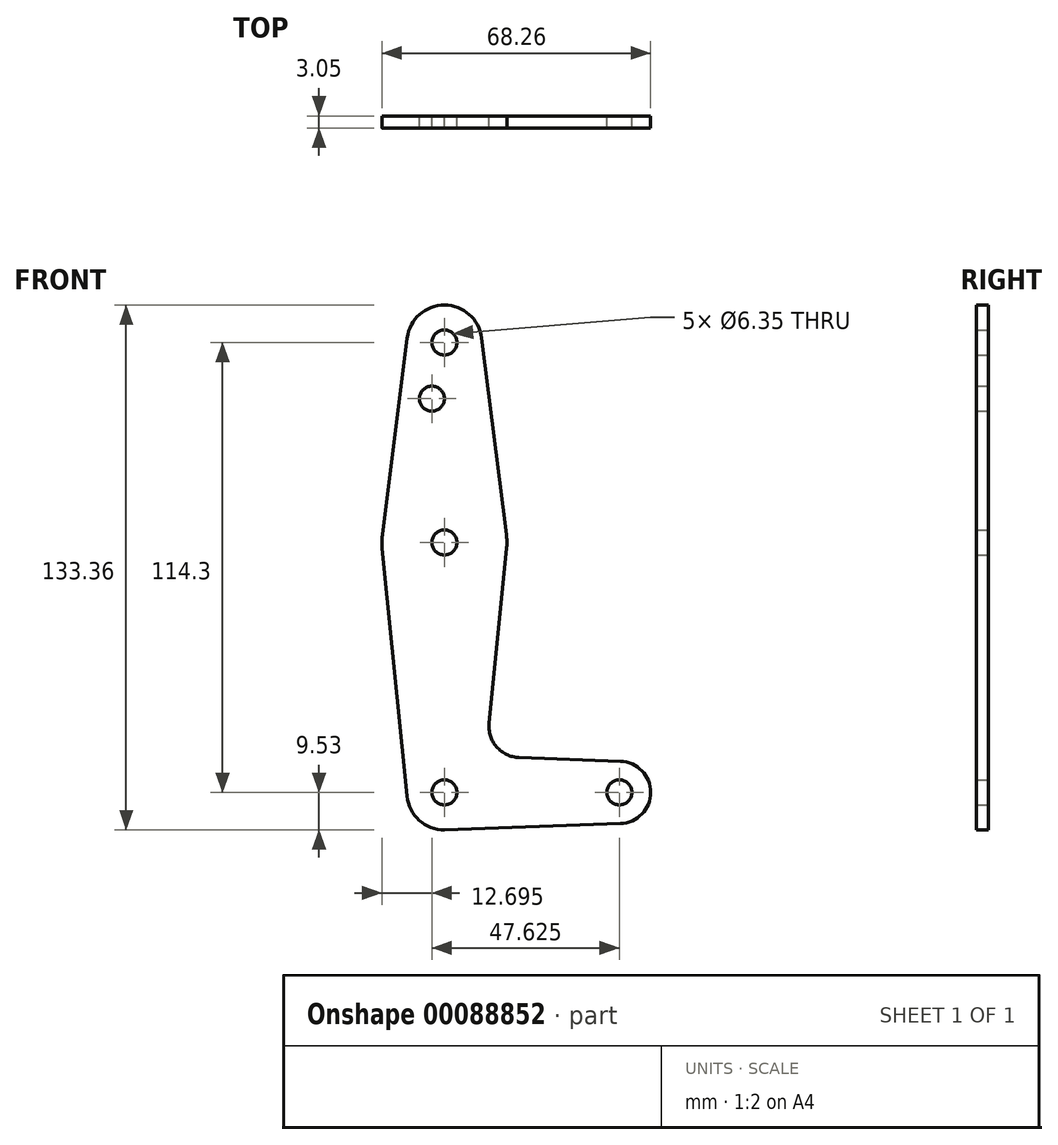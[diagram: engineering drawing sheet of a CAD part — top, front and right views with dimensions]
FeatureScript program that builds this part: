
annotation { "Feature Type Name" : "Feature", "Feature Type Description" : "" }
export const myFeature = defineFeature(function(context is Context, id is Id, definition is map)
    precondition{}
    {
        {
            var Q0;
            Q0=qCreatedBy(makeId("Front.planeOp"),FACE);
            var sketch = newSketch(context, id + "F0", { "sketchPlane" : qUnion([Q0])});
            skCircle(sketch, "E0", {"center": v(0, 114.3) * mm, "radius": 9.53 * mm});
            skLineSegment(sketch, "E1", {"start": v(0, 114.3) * mm, "end": v(0, 63.5) * mm, "construction": true});
            skCircle(sketch, "E2", {"center": v(0, 63.5) * mm, "radius": 15.88 * mm});
            skLineSegment(sketch, "E3", {"start": v(0, 63.5) * mm, "end": v(0, 0) * mm, "construction": true});
            skCircle(sketch, "E4", {"center": v(0, 0) * mm, "radius": 9.53 * mm});
            skLineSegment(sketch, "E5", {"start": v(0, 0) * mm, "end": v(44.45, 0) * mm, "construction": true});
            skCircle(sketch, "E6", {"center": v(44.45, 0) * mm, "radius": 7.94 * mm});
            skLineSegment(sketch, "E7", {"start": v(-9.45, 115.5) * mm, "end": v(-15.75, 65.48) * mm});
            skLineSegment(sketch, "E8", {"start": v(9.45, 115.5) * mm, "end": v(15.75, 65.48) * mm});
            skLineSegment(sketch, "E9", {"start": v(-15.8, 61.91) * mm, "end": v(-9.48, -0.95) * mm});
            skLineSegment(sketch, "E10", {"start": v(15.8, 61.91) * mm, "end": v(11.34, 17.6) * mm});
            skLineSegment(sketch, "E11", {"start": v(0, -9.53) * mm, "end": v(44.73, -7.93) * mm});
            skLineSegment(sketch, "E12", {"start": v(44.73, 7.93) * mm, "end": v(18.97, 8.85) * mm});
            skArc(sketch, "E13.filletArc", {"start": v(11.34, 17.6) * mm, "mid": v(13.26, 11.57) * mm, "end": v(18.97, 8.85) * mm});
            skCircle(sketch, "E14", {"center": v(-3.18, 100.03) * mm, "radius": 3.18 * mm});
            skCircle(sketch, "E15", {"center": v(0, 114.3) * mm, "radius": 3.18 * mm});
            skCircle(sketch, "E16", {"center": v(0, 63.5) * mm, "radius": 3.18 * mm});
            skCircle(sketch, "E17", {"center": v(0, 0) * mm, "radius": 3.18 * mm});
            skCircle(sketch, "E18", {"center": v(44.45, 0) * mm, "radius": 3.18 * mm});
            skSolve(sketch);
        }
        {
            var Q0;
            {var subQ1=sQuery(id+"F0.wireOp",EDGE,"E7");Q0=makeQuery(id+"F0.imprint","IMPRINT",FACE,{"disambiguationData":[TD([[makeQuery(id+"F0.imprint","IMPRINT",EDGE,{"derivedFrom":subQ1}),1.0]])]});}
            var Q1;
            Q1=makeQuery(id+"F0.imprint","IMPRINT",FACE,{"disambiguationData":[TD([[makeQuery(id+"F0.imprint","IMPRINT",EDGE,{"derivedFrom":sQuery(id+"F0.wireOp",EDGE,"E16")}),-1.0]])]});
            var Q2;
            Q2=makeQuery(id+"F0.imprint","IMPRINT",FACE,{"disambiguationData":[TD([[makeQuery(id+"F0.imprint","IMPRINT",EDGE,{"derivedFrom":sQuery(id+"F0.wireOp",EDGE,"E15")}),-1.0]])]});
            var Q3;
            {var subQ0=sQuery(id+"F0.wireOp",EDGE,"E9");Q3=makeQuery(id+"F0.imprint","IMPRINT",FACE,{"disambiguationData":[TD([[makeQuery(id+"F0.imprint","IMPRINT",EDGE,{"derivedFrom":subQ0}),1.0]])]});}
            var Q4;
            Q4=makeQuery(id+"F0.imprint","IMPRINT",FACE,{"disambiguationData":[TD([[makeQuery(id+"F0.imprint","IMPRINT",EDGE,{"derivedFrom":sQuery(id+"F0.wireOp",EDGE,"E17")}),-1.0]])]});
            var Q5;
            Q5=makeQuery(id+"F0.imprint","IMPRINT",FACE,{"disambiguationData":[TD([[makeQuery(id+"F0.imprint","IMPRINT",EDGE,{"derivedFrom":sQuery(id+"F0.wireOp",EDGE,"E18")}),-1.0]])]});
            extrude(context, id + "F1", {"entities" : qUnion([Q0, Q1, Q2, Q3, Q4, Q5]), "depth" : 3.05 * mm});
        }
    });
